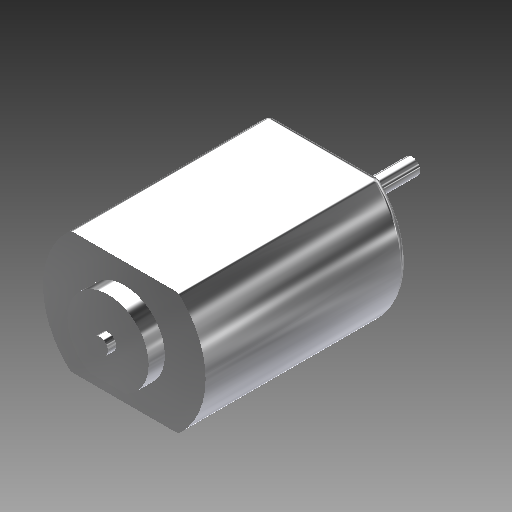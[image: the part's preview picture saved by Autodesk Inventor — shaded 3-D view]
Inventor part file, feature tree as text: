
AUTODESK INVENTOR PART (.ipt)
format: ipt  version: 2017 (Build 210142000, 142)  size: 200,704 bytes
history: native  units: mm
features: extrude x5, sketch x5, fillet x4
ambient origin geometry x8: Origin, YZ Plane, XZ Plane, XY Plane, X Axis, Y Axis, Z Axis, Center Point
bodies: Solid1 (feature_tree)
feature tree (14):
  extrude  "Extrusion1"  Depth=8.4mm TaperAngle=0.0deg
  extrude  "Extrusion2"  Depth=2.0mm TaperAngle=0.0deg
  extrude  "Extrusion3"  Depth=10.0mm
  extrude  "Extrusion4"  Depth=2.0mm
  extrude  "Extrusion5"  Depth=1.0mm
  fillet  "Fillet7"  Radius=1.0mm
  fillet  "Fillet8"  Radius=1.0mm
  fillet  "Fillet9"  Radius=1.0mm
  fillet  "Fillet10"  Radius=1.0mm
  sketch  "Sketch1"  dims[d0=2.0mm d1=8.4mm d2=0.0mm]
  sketch  "Sketch2"  dims[d3=6.0mm d4=2.0mm d5=0.0mm]
  sketch  "Sketch3"  dims[d8=25.0mm d9=0.0mm d10=10.0mm]
  sketch  "Sketch4"  dims[d12=2.0mm d13=0.0mm d14=2.0mm]
  sketch  "Sketch5"  dims[d15=1.0mm d16=0.0mm d23=20.0mm d24=1.0mm d25=1.0mm d26=1.0mm d27=1.0mm]
